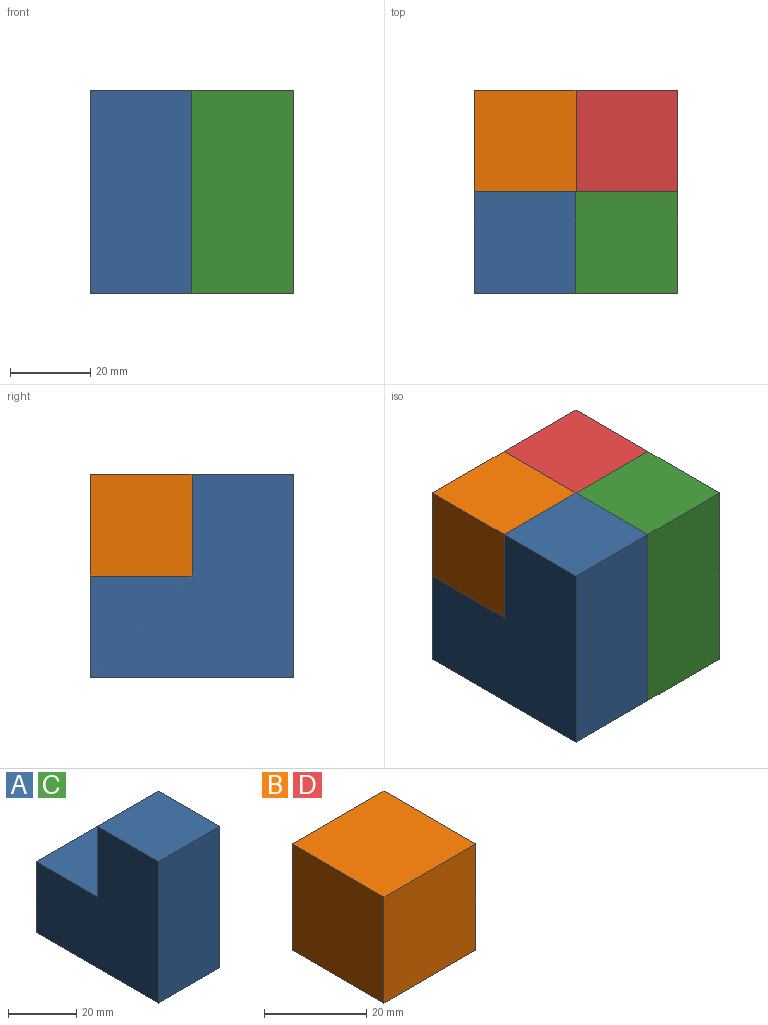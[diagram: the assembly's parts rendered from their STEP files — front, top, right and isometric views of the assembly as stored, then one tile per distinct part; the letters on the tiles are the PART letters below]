
ASSEMBLY  parts=4 mates=3
PART A: 8 faces, bbox 25.4x50.8x50.8 mm
  f0: plane 25.4x25.4mm, normal (0,0,1), area 645.2mm2, adj f1,f3,f4,f6
  f1: plane 50.8x50.8mm, normal (-1,0,0), area 1935.5mm2, adj f0,f2,f4,f5,f6,f7
  f2: plane 50.8x25.4mm, normal (0,-1,0), area 1290.3mm2, adj f1,f3,f5,f7
  f3: plane 50.8x50.8mm, normal (1,0,0), area 1935.5mm2, adj f0,f2,f4,f5,f6,f7
  f4: plane 25.4x25.4mm, normal (0,1,0), area 645.2mm2, adj f0,f1,f3,f5
  f5: plane 50.8x25.4mm, normal (0,0,-1), area 1290.3mm2, adj f1,f2,f3,f4
  f6: plane 25.4x25.4mm, normal (0,1,0), area 645.2mm2, adj f0,f1,f3,f7
  f7: plane 25.4x25.4mm, normal (0,0,1), area 645.2mm2, adj f1,f2,f3,f6
PART B: 6 faces, bbox 25.4x25.4x25.4 mm
  f0: plane 25.4x25.4mm, normal (-1,0,0), area 645.2mm2, adj f1,f3,f4,f5
  f1: plane 25.4x25.4mm, normal (0,-1,0), area 645.2mm2, adj f0,f2,f4,f5
  f2: plane 25.4x25.4mm, normal (1,0,0), area 645.2mm2, adj f1,f3,f4,f5
  f3: plane 25.4x25.4mm, normal (0,1,0), area 645.2mm2, adj f0,f2,f4,f5
  f4: plane 25.4x25.4mm, normal (0,0,1), area 645.2mm2, adj f0,f1,f2,f3
  f5: plane 25.4x25.4mm, normal (0,0,-1), area 645.2mm2, adj f0,f1,f2,f3
PART C: same geometry as A
PART D: same geometry as B
PLACE A t=(-19.45,-14.46,-4.84)mm
PLACE B t=(-32.81,-25.36,20.56)mm
PLACE C t=(5.95,-14.46,-4.84)mm
PLACE D t=(-7.41,-25.36,20.56)mm
MATE fastened B.f2 <-> A.f3  axis (1,0,0) through (-12.31,-15.71,20.56)mm
MATE fastened D.f2 <-> C.f3  axis (1,0,0) through (13.09,-15.71,20.56)mm
MATE fastened C.f2 <-> A.f2  axis (0,-1,0) through (-12.31,-41.11,20.56)mm
